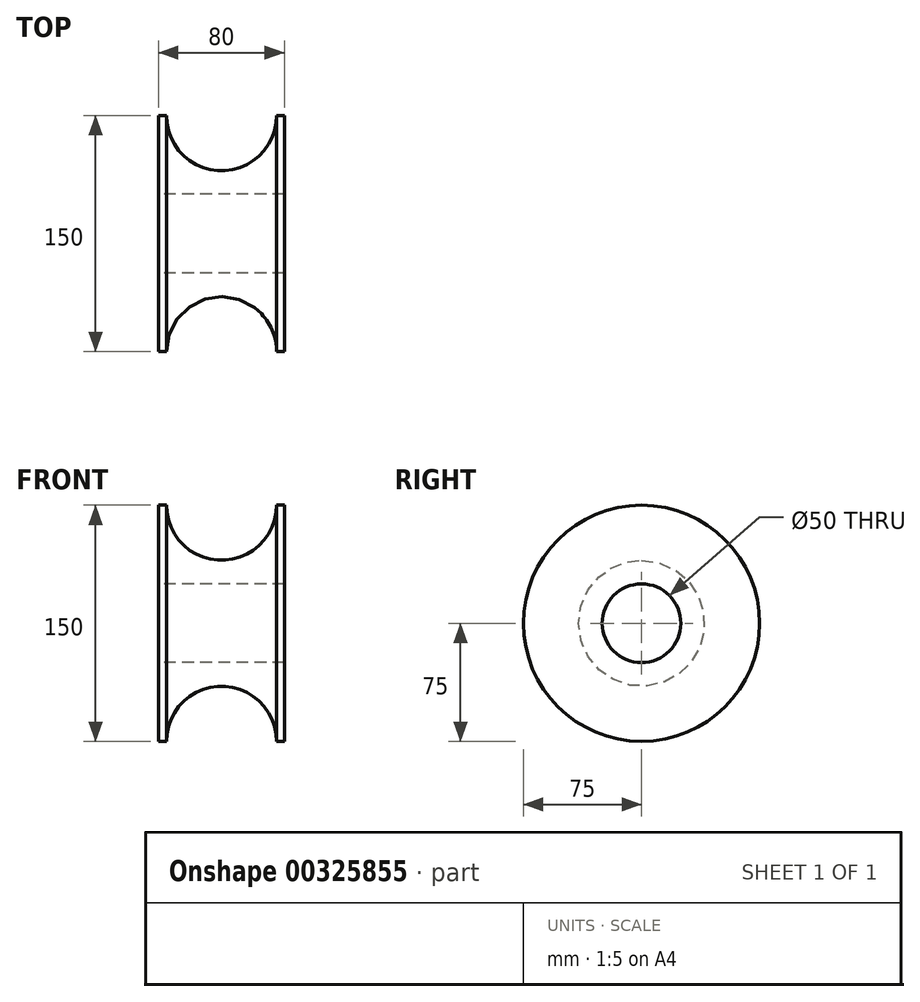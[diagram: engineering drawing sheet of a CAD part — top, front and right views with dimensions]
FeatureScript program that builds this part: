
annotation { "Feature Type Name" : "Feature", "Feature Type Description" : "" }
export const myFeature = defineFeature(function(context is Context, id is Id, definition is map)
    precondition{}
    {
        {
            var Q0;
            Q0=qCreatedBy(makeId("Right.planeOp"),FACE);
            var sketch = newSketch(context, id + "F0", { "sketchPlane" : qUnion([Q0])});
            skCircle(sketch, "E0", {"center": v(0, 0) * mm, "radius": 75 * mm});
            skSolve(sketch);
        }
        {
            var Q0;
            Q0 = qSketchRegion(id + "F0", true);
            extrude(context, id + "F1", {"entities" : qUnion([Q0]), "depth" : 80 * mm});
        }
        {
            var Q0;
            Q0=makeQuery(id+"F1.opExtrude","CAP_FACE",FACE,{"disambiguationData":[OSD([sQuery(id+"F0.wireOp",EDGE,"E0")])],"isStart":true});
            var sketch = newSketch(context, id + "F2", { "sketchPlane" : qUnion([Q0])});
            skCircle(sketch, "E1", {"center": v(0, 0) * mm, "radius": 25 * mm});
            skSolve(sketch);
        }
        {
            var Q0;
            Q0=makeQuery(id+"F2.imprint","IMPRINT",FACE,{"disambiguationData":[TD([[makeQuery(id+"F2.imprint","IMPRINT",EDGE,{"derivedFrom":sQuery(id+"F2.wireOp",EDGE,"E1")}),1.0]])]});
            extrude(context, id + "F3", {"entities" : qUnion([Q0]), "operationType" : NewBodyOperationType.REMOVE, "oppositeDirection" : true, "depth" : 100 * mm});
        }
        {
            var Q0;
            Q0=qCreatedBy(makeId("Top.planeOp"),FACE);
            var sketch = newSketch(context, id + "F4", { "sketchPlane" : qUnion([Q0])});
            skCircle(sketch, "E2", {"center": v(40, -75) * mm, "radius": 35 * mm});
            skSolve(sketch);
        }
        {
            var Q0;
            Q0=makeQuery(id+"F4.imprint","IMPRINT",FACE,{"disambiguationData":[TD([[makeQuery(id+"F4.imprint","IMPRINT",EDGE,{"derivedFrom":sQuery(id+"F4.wireOp",EDGE,"E2")}),1.0]])]});
            var Q1;
            Q1=makeQuery(id+"F1.opExtrude","SWEPT_FACE",FACE,{"disambiguationData":[OSD([sQuery(id+"F0.wireOp",EDGE,"E0")])]});
            revolve(context, id + "F5", {"operationType" : NewBodyOperationType.REMOVE, "entities" : qUnion([Q0]), "axis" : qUnion([Q1]), "revolveType" : RevolveType.FULL, "oppositeDirection" : true});
        }
    });
